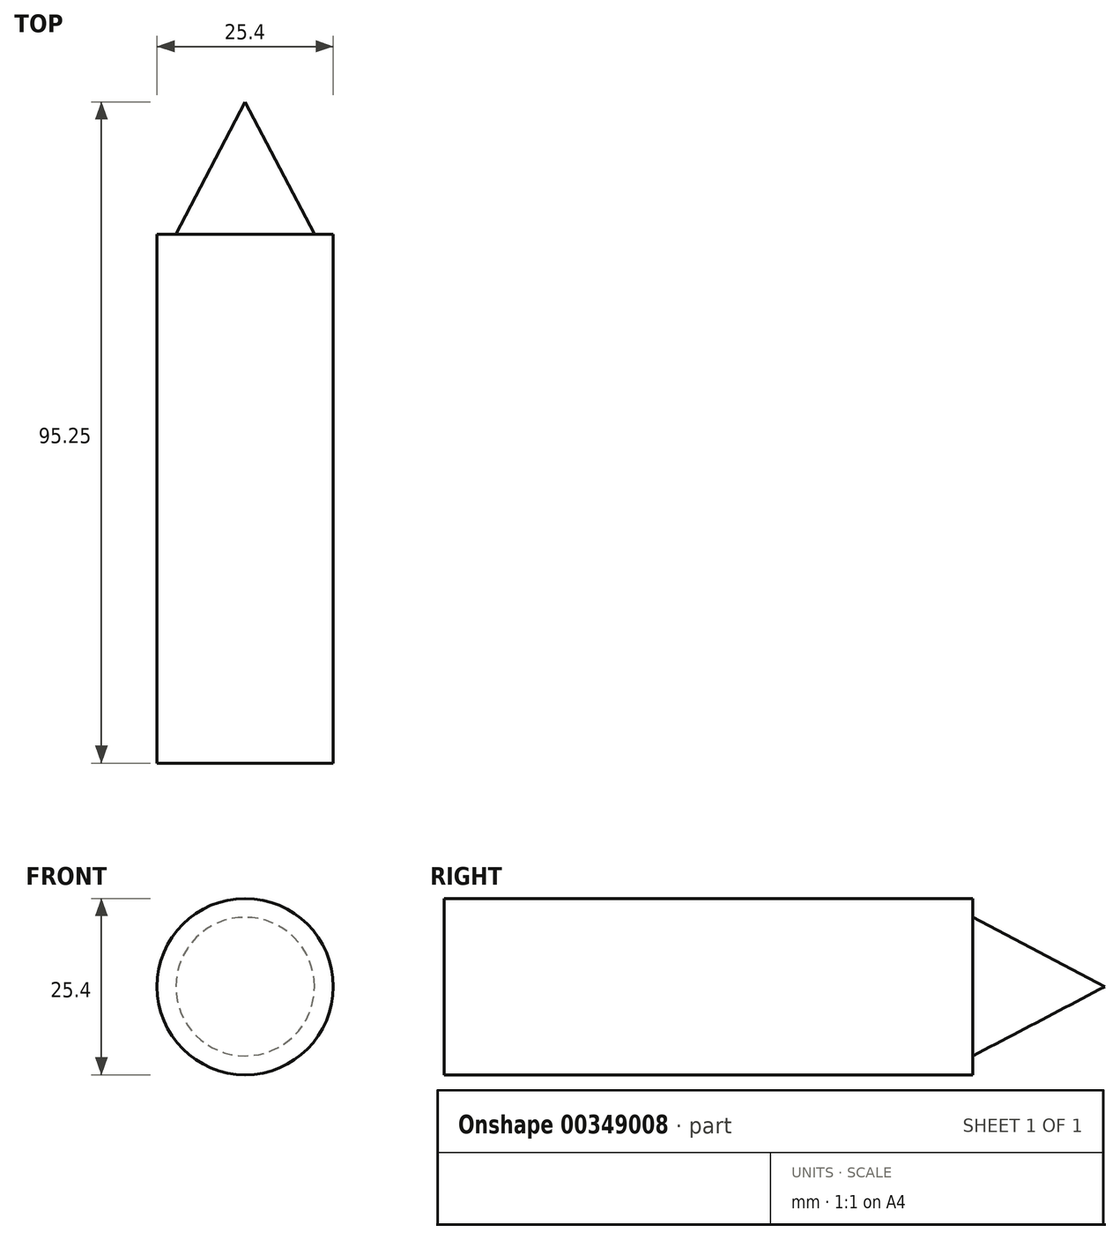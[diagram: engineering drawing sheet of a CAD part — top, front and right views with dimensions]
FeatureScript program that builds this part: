
annotation { "Feature Type Name" : "Feature", "Feature Type Description" : "" }
export const myFeature = defineFeature(function(context is Context, id is Id, definition is map)
    precondition{}
    {
        {
            var Q0;
            Q0=qCreatedBy(makeId("Top.planeOp"),FACE);
            var sketch = newSketch(context, id + "F0", { "sketchPlane" : qUnion([Q0])});
            skLineSegment(sketch, "E0", {"start": v(0, 0) * mm, "end": v(0, 0) * mm});
            skLineSegment(sketch, "E1", {"start": v(0, -76.2) * mm, "end": v(0, 0) * mm});
            skLineSegment(sketch, "E2", {"start": v(0, -76.2) * mm, "end": v(12.7, -76.2) * mm});
            skLineSegment(sketch, "E3", {"start": v(12.7, -76.2) * mm, "end": v(12.7, -76.2) * mm});
            skLineSegment(sketch, "E4", {"start": v(12.7, -76.2) * mm, "end": v(12.7, 0) * mm});
            skLineSegment(sketch, "E5", {"start": v(12.7, 0) * mm, "end": v(12.7, 0) * mm});
            skLineSegment(sketch, "E6", {"start": v(0, 0) * mm, "end": v(0, 19.05) * mm});
            skLineSegment(sketch, "E7", {"start": v(0, 19.05) * mm, "end": v(0, 19.05) * mm});
            skLineSegment(sketch, "E8", {"start": v(0, 19.05) * mm, "end": v(9.98, 0) * mm});
            skLineSegment(sketch, "E9", {"start": v(9.98, 0) * mm, "end": v(12.7, 0) * mm});
            skSolve(sketch);
        }
        {
            var Q0;
            Q0 = qSketchRegion(id + "F0", true);
            var Q1;
            Q1=sQuery(id+"F0.wireOp",EDGE,"E1");
            revolve(context, id + "F1", {"entities" : qUnion([Q0]), "axis" : qUnion([Q1]), "revolveType" : RevolveType.FULL});
        }
    });
